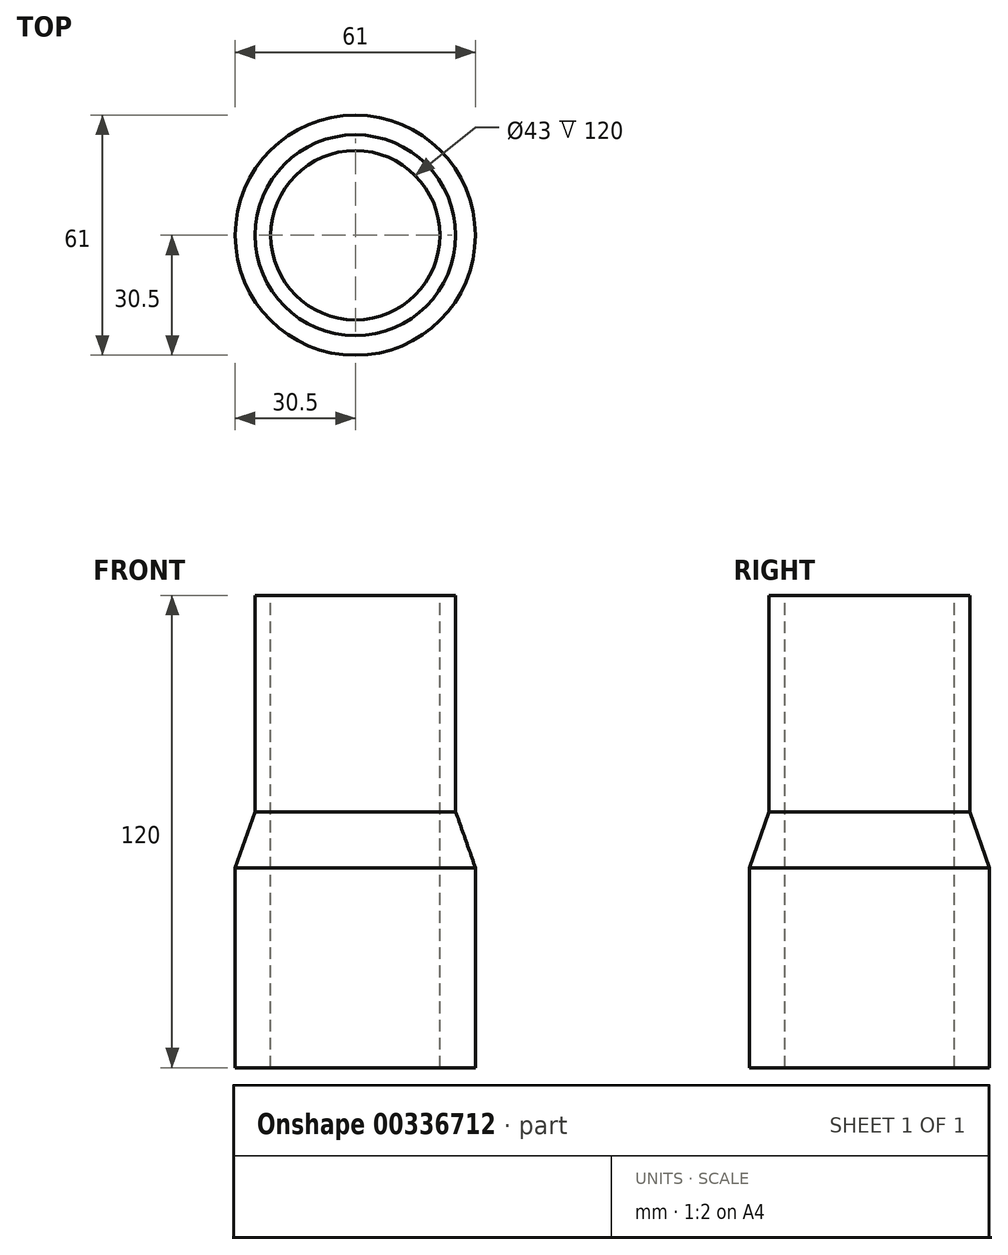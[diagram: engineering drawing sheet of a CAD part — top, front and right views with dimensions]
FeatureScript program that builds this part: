
annotation { "Feature Type Name" : "Feature", "Feature Type Description" : "" }
export const myFeature = defineFeature(function(context is Context, id is Id, definition is map)
    precondition{}
    {
        {
            var Q0;
            Q0=qCreatedBy(makeId("Front.planeOp"),FACE);
            var sketch = newSketch(context, id + "F0", { "sketchPlane" : qUnion([Q0])});
            skLineSegment(sketch, "E0", {"start": v(0, 44.96) * mm, "end": v(0, -75.04) * mm, "construction": true});
            skLineSegment(sketch, "E1", {"start": v(21.5, -75.04) * mm, "end": v(30.5, -75.04) * mm});
            skLineSegment(sketch, "E2", {"start": v(30.5, -75.04) * mm, "end": v(30.5, -24.24) * mm});
            skLineSegment(sketch, "E3", {"start": v(30.5, -24.24) * mm, "end": v(25.5, -10.04) * mm});
            skLineSegment(sketch, "E4", {"start": v(25.5, -10.04) * mm, "end": v(25.5, 44.96) * mm});
            skLineSegment(sketch, "E5", {"start": v(25.5, 44.96) * mm, "end": v(21.5, 44.96) * mm});
            skLineSegment(sketch, "E6", {"start": v(21.5, 44.96) * mm, "end": v(21.5, -75.04) * mm});
            skSolve(sketch);
        }
        {
            var Q0;
            Q0=makeQuery(id+"F0.imprint","IMPRINT",FACE,{"disambiguationData":[TD([[makeQuery(id+"F0.imprint","IMPRINT",EDGE,{"derivedFrom":sQuery(id+"F0.wireOp",EDGE,"E1")}),1.0]])]});
            var Q1;
            Q1=sQuery(id+"F0.wireOp",EDGE,"E0");
            revolve(context, id + "F1", {"entities" : qUnion([Q0]), "axis" : qUnion([Q1]), "revolveType" : RevolveType.FULL});
        }
    });
